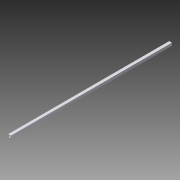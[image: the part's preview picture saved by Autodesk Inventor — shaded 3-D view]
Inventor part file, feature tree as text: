
AUTODESK INVENTOR PART (.ipt)
format: ipt  version: 2015 (Build 190159000, 159)  size: 90,624 bytes
history: native  units: in
note: dims shown in document units (in); Inventor stores cm internally (conversion verified against a paired STEP export)
features: extrude x2, sketch x2
ambient origin geometry x8: Origin, YZ Plane, XZ Plane, XY Plane, X Axis, Y Axis, Z Axis, Center Point
bodies: Solid1 (feature_tree)
feature tree (4):
  extrude  "Extrusion1"  Depth=0.125in
  extrude  "Extrusion2"  TaperAngle=0.0deg  [1 undecoded]
  sketch  "Sketch1"  dims[d0=1.0in d1=0.125in]
  sketch  "Sketch2"  dims[d2=59.1352in d3=0.0in d4=58.1352in d5=0.25in d6=59.1352in d7=0.0in]
note: 1 required parameter value undecoded (feature->parameter linkage not recoverable at this tier; creation-order binding heuristic only, values carry confidence <= 0.55)
